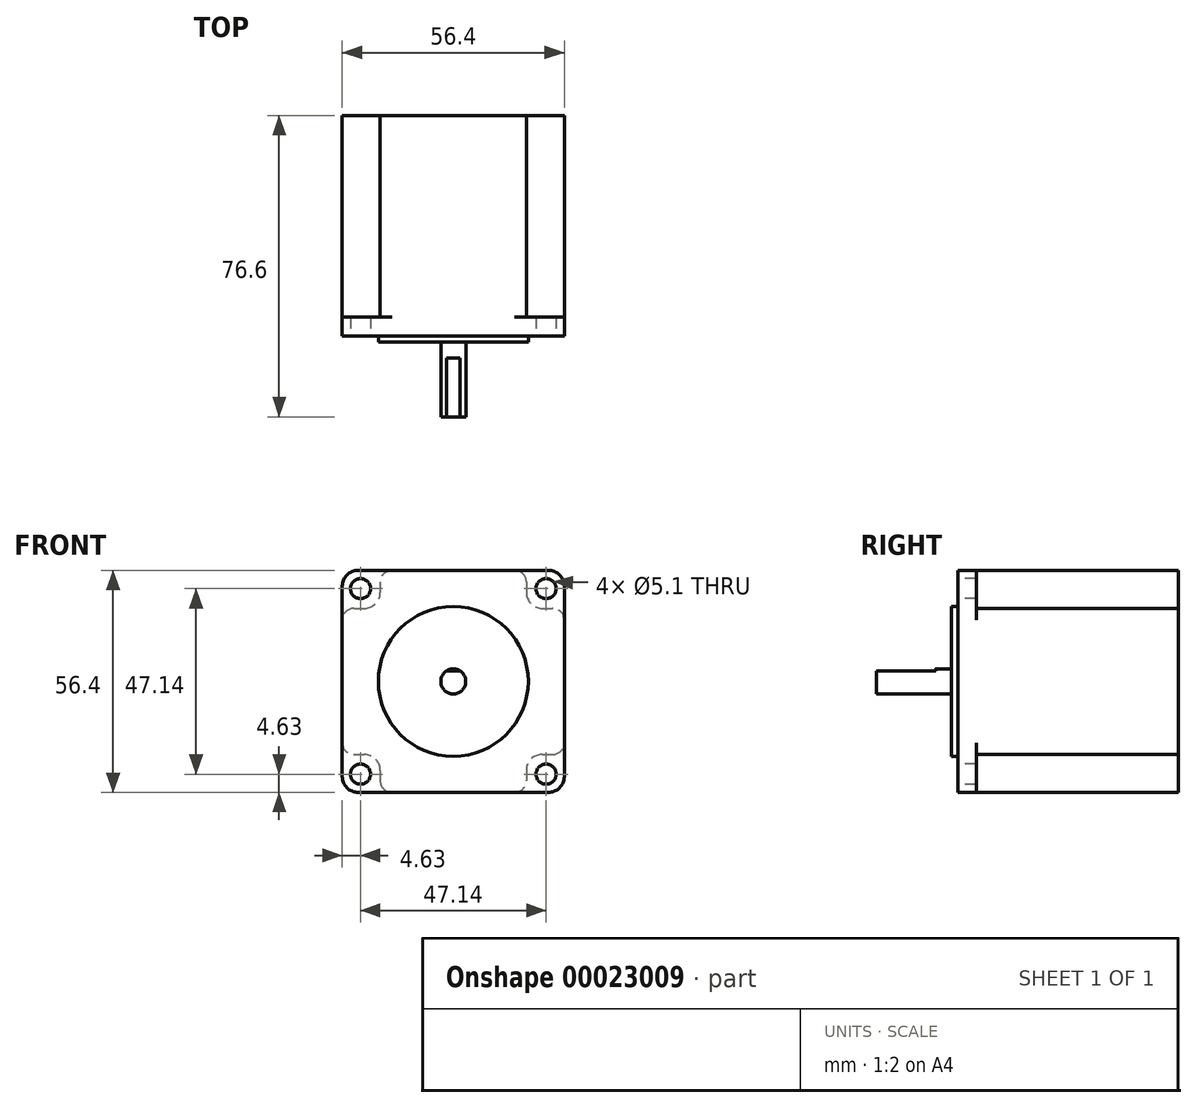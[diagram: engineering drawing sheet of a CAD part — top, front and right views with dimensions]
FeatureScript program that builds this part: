
annotation { "Feature Type Name" : "Feature", "Feature Type Description" : "" }
export const myFeature = defineFeature(function(context is Context, id is Id, definition is map)
    precondition{}
    {
        {
            var Q0;
            Q0=qCreatedBy(makeId("Front.planeOp"),FACE);
            var sketch = newSketch(context, id + "F0", { "sketchPlane" : qUnion([Q0])});
            skLineSegment(sketch, "E0.rect.bottom", {"start": v(-28.2, 28.2) * mm, "end": v(28.2, 28.2) * mm});
            skLineSegment(sketch, "E0.rect.top", {"start": v(-28.2, -28.2) * mm, "end": v(28.2, -28.2) * mm});
            skLineSegment(sketch, "E0.rect.left", {"start": v(-28.2, 28.2) * mm, "end": v(-28.2, -28.2) * mm});
            skLineSegment(sketch, "E0.rect.right", {"start": v(28.2, 28.2) * mm, "end": v(28.2, -28.2) * mm});
            skPoint(sketch, "E0.rect.middle", {"position": v(0, 0) * mm});
            skCircle(sketch, "E1", {"center": v(0, 0) * mm, "radius": 19.05 * mm});
            skCircle(sketch, "E2", {"center": v(0, 0) * mm, "radius": 3.17 * mm});
            skCircle(sketch, "E3", {"center": v(-23.57, 23.57) * mm, "radius": 2.55 * mm});
            skCircle(sketch, "E4", {"center": v(23.57, 23.57) * mm, "radius": 2.55 * mm});
            skCircle(sketch, "E5", {"center": v(23.57, -23.57) * mm, "radius": 2.55 * mm});
            skCircle(sketch, "E6", {"center": v(-23.57, -23.57) * mm, "radius": 2.55 * mm});
            skLineSegment(sketch, "E7.rect.bottom", {"start": v(-23.57, 23.57) * mm, "end": v(23.57, 23.57) * mm, "construction": true});
            skLineSegment(sketch, "E7.rect.top", {"start": v(-23.57, -23.57) * mm, "end": v(23.57, -23.57) * mm, "construction": true});
            skLineSegment(sketch, "E7.rect.left", {"start": v(-23.57, 23.57) * mm, "end": v(-23.57, -23.57) * mm, "construction": true});
            skLineSegment(sketch, "E7.rect.right", {"start": v(23.57, 23.57) * mm, "end": v(23.57, -23.57) * mm, "construction": true});
            skSolve(sketch);
        }
        {
            var Q0;
            Q0=makeQuery(id+"F0.imprint","IMPRINT",FACE,{"disambiguationData":[TD([[makeQuery(id+"F0.imprint","IMPRINT",EDGE,{"derivedFrom":sQuery(id+"F0.wireOp",EDGE,"E0.rect.bottom")}),-1.0]])]});
            var Q1;
            Q1=makeQuery(id+"F0.imprint","IMPRINT",FACE,{"disambiguationData":[TD([[makeQuery(id+"F0.imprint","IMPRINT",EDGE,{"derivedFrom":sQuery(id+"F0.wireOp",EDGE,"E1")}),1.0]])]});
            var Q2;
            Q2=makeQuery(id+"F0.imprint","IMPRINT",FACE,{"disambiguationData":[TD([[makeQuery(id+"F0.imprint","IMPRINT",EDGE,{"derivedFrom":sQuery(id+"F0.wireOp",EDGE,"E2")}),1.0]])]});
            extrude(context, id + "F1", {"entities" : qUnion([Q0, Q1, Q2]), "oppositeDirection" : true, "depth" : 4.8 * mm});
        }
        {
            var Q0;
            Q0=makeQuery(id+"F0.imprint","IMPRINT",FACE,{"disambiguationData":[TD([[makeQuery(id+"F0.imprint","IMPRINT",EDGE,{"derivedFrom":sQuery(id+"F0.wireOp",EDGE,"E1")}),1.0]])]});
            extrude(context, id + "F2", {"entities" : qUnion([Q0]), "operationType" : NewBodyOperationType.ADD, "depth" : 1.6 * mm});
        }
        {
            var Q0;
            Q0=makeQuery(id+"F0.imprint","IMPRINT",FACE,{"disambiguationData":[TD([[makeQuery(id+"F0.imprint","IMPRINT",EDGE,{"derivedFrom":sQuery(id+"F0.wireOp",EDGE,"E2")}),1.0]])]});
            extrude(context, id + "F3", {"entities" : qUnion([Q0]), "operationType" : NewBodyOperationType.ADD, "depth" : 20.6 * mm});
        }
        {
            var Q0;
            Q0=makeQuery(id+"F1.opExtrude","SWEPT_EDGE",EDGE,{"disambiguationData":[OSD([sQuery(id+"F0.wireOp",EDGE,"E0.rect.bottom"),sQuery(id+"F0.wireOp",EDGE,"E0.rect.left")])]});
            var Q1;
            Q1=makeQuery(id+"F1.opExtrude","SWEPT_EDGE",EDGE,{"disambiguationData":[OSD([sQuery(id+"F0.wireOp",EDGE,"E0.rect.bottom"),sQuery(id+"F0.wireOp",EDGE,"E0.rect.right")])]});
            var Q2;
            Q2=makeQuery(id+"F1.opExtrude","SWEPT_EDGE",EDGE,{"disambiguationData":[OSD([sQuery(id+"F0.wireOp",EDGE,"E0.rect.top"),sQuery(id+"F0.wireOp",EDGE,"E0.rect.right")])]});
            var Q3;
            Q3=makeQuery(id+"F1.opExtrude","SWEPT_EDGE",EDGE,{"disambiguationData":[OSD([sQuery(id+"F0.wireOp",EDGE,"E0.rect.top"),sQuery(id+"F0.wireOp",EDGE,"E0.rect.left")])]});
            fillet(context, id + "F4", {"entities" : qUnion([Q0, Q1, Q2, Q3]), "radius" : 4 * mm, "tangentPropagation" : true, "allowEdgeOverflow" : false});
        }
        {
            var Q0;
            Q0=makeQuery(id+"F1.opExtrude","SWEPT_FACE",FACE,{"disambiguationData":[OSD([sQuery(id+"F0.wireOp",EDGE,"E0.rect.left")])]});
            var sketch = newSketch(context, id + "F5", { "sketchPlane" : qUnion([Q0])});
            skLineSegment(sketch, "E8", {"start": v(1.6, 3.17) * mm, "end": v(20.6, 3.17) * mm});
            skLineSegment(sketch, "E9.0", {"start": v(20.6, 3.17) * mm, "end": v(20.6, -3.17) * mm});
            skLineSegment(sketch, "E10", {"start": v(5.6, 3.17) * mm, "end": v(5.6, 2.67) * mm});
            skLineSegment(sketch, "E11", {"start": v(5.6, 2.67) * mm, "end": v(20.6, 2.67) * mm});
            skSolve(sketch);
        }
        {
            var Q0;
            {var subQ1=sQuery(id+"F5.wireOp",EDGE,"E10");Q0=makeQuery(id+"F5.imprint","IMPRINT",FACE,{"disambiguationData":[TD([[makeQuery(id+"F5.imprint","IMPRINT",EDGE,{"derivedFrom":subQ1}),1.0]])]});}
            extrude(context, id + "F6", {"entities" : qUnion([Q0]), "operationType" : NewBodyOperationType.REMOVE, "endBound" : BoundingType.THROUGH_ALL, "oppositeDirection" : true, "depth" : 25 * mm});
        }
        {
            var Q0;
            Q0=qCreatedBy(makeId("Front.planeOp"),FACE);
            var sketch = newSketch(context, id + "F7", { "sketchPlane" : qUnion([Q0])});
            skPoint(sketch, "E12.rect.middle", {"position": v(0, 0.02) * mm});
            skPoint(sketch, "E13", {"position": v(0, 0) * mm});
            skLineSegment(sketch, "E14.rect.bottom", {"start": v(-18.57, 28.2) * mm, "end": v(18.57, 28.2) * mm});
            skLineSegment(sketch, "E14.rect.top", {"start": v(-18.57, -28.2) * mm, "end": v(18.57, -28.2) * mm});
            skLineSegment(sketch, "E14.rect.left", {"start": v(-18.57, 28.2) * mm, "end": v(-18.57, -28.2) * mm});
            skLineSegment(sketch, "E14.rect.right", {"start": v(18.57, 28.2) * mm, "end": v(18.57, -28.2) * mm});
            skLineSegment(sketch, "E15.rect.bottom", {"start": v(-28.2, 18.57) * mm, "end": v(28.2, 18.57) * mm});
            skLineSegment(sketch, "E15.rect.top", {"start": v(-28.2, -18.57) * mm, "end": v(28.2, -18.57) * mm});
            skLineSegment(sketch, "E15.rect.left", {"start": v(-28.2, 18.57) * mm, "end": v(-28.2, -18.57) * mm});
            skLineSegment(sketch, "E15.rect.right", {"start": v(28.2, 18.57) * mm, "end": v(28.2, -18.57) * mm});
            skSolve(sketch);
        }
        {
            var Q0;
            Q0=qSketchRegion(id+"F7",true);
            extrude(context, id + "F8", {"entities" : qUnion([Q0]), "operationType" : NewBodyOperationType.ADD, "oppositeDirection" : true, "depth" : 56 * mm});
        }
        {
            var Q0;
            Q0=makeQuery(id+"F8.opExtrude","SWEPT_EDGE",EDGE,{"disambiguationData":[OSD([sQuery(id+"F7.wireOp",EDGE,"E14.rect.right"),sQuery(id+"F7.wireOp",EDGE,"E15.rect.bottom")])]});
            var Q1;
            Q1=makeQuery(id+"F8.opExtrude","SWEPT_EDGE",EDGE,{"disambiguationData":[OSD([sQuery(id+"F7.wireOp",EDGE,"E14.rect.left"),sQuery(id+"F7.wireOp",EDGE,"E15.rect.bottom")])]});
            var Q2;
            Q2=makeQuery(id+"F8.opExtrude","SWEPT_EDGE",EDGE,{"disambiguationData":[OSD([sQuery(id+"F7.wireOp",EDGE,"E14.rect.left"),sQuery(id+"F7.wireOp",EDGE,"E15.rect.top")])]});
            var Q3;
            Q3=makeQuery(id+"F8.opExtrude","SWEPT_EDGE",EDGE,{"disambiguationData":[OSD([sQuery(id+"F7.wireOp",EDGE,"E14.rect.right"),sQuery(id+"F7.wireOp",EDGE,"E15.rect.top")])]});
            fillet(context, id + "F9", {"entities" : qUnion([Q0, Q1, Q2, Q3]), "radius" : 4 * mm, "tangentPropagation" : true, "allowEdgeOverflow" : false});
        }
        {
            var Q0;
            Q0=makeQuery(id+"F8.opExtrude","SWEPT_EDGE",EDGE,{"disambiguationData":[OSD([sQuery(id+"F7.wireOp",EDGE,"E14.rect.bottom"),sQuery(id+"F7.wireOp",EDGE,"E14.rect.right")])]});
            var Q1;
            Q1=makeQuery(id+"F8.opExtrude","SWEPT_EDGE",EDGE,{"disambiguationData":[OSD([sQuery(id+"F7.wireOp",EDGE,"E15.rect.bottom"),sQuery(id+"F7.wireOp",EDGE,"E15.rect.right")])]});
            var Q2;
            Q2=makeQuery(id+"F8.opExtrude","SWEPT_EDGE",EDGE,{"disambiguationData":[OSD([sQuery(id+"F7.wireOp",EDGE,"E15.rect.top"),sQuery(id+"F7.wireOp",EDGE,"E15.rect.right")])]});
            var Q3;
            Q3=makeQuery(id+"F8.opExtrude","SWEPT_EDGE",EDGE,{"disambiguationData":[OSD([sQuery(id+"F7.wireOp",EDGE,"E14.rect.top"),sQuery(id+"F7.wireOp",EDGE,"E14.rect.right")])]});
            var Q4;
            Q4=makeQuery(id+"F8.opExtrude","SWEPT_EDGE",EDGE,{"disambiguationData":[OSD([sQuery(id+"F7.wireOp",EDGE,"E14.rect.top"),sQuery(id+"F7.wireOp",EDGE,"E14.rect.left")])]});
            var Q5;
            Q5=makeQuery(id+"F8.opExtrude","SWEPT_EDGE",EDGE,{"disambiguationData":[OSD([sQuery(id+"F7.wireOp",EDGE,"E15.rect.top"),sQuery(id+"F7.wireOp",EDGE,"E15.rect.left")])]});
            var Q6;
            Q6=makeQuery(id+"F8.opExtrude","SWEPT_EDGE",EDGE,{"disambiguationData":[OSD([sQuery(id+"F7.wireOp",EDGE,"E15.rect.bottom"),sQuery(id+"F7.wireOp",EDGE,"E15.rect.left")])]});
            var Q7;
            Q7=makeQuery(id+"F8.opExtrude","SWEPT_EDGE",EDGE,{"disambiguationData":[OSD([sQuery(id+"F7.wireOp",EDGE,"E14.rect.bottom"),sQuery(id+"F7.wireOp",EDGE,"E14.rect.left")])]});
            fillet(context, id + "F10", {"entities" : qUnion([Q0, Q1, Q2, Q3, Q4, Q5, Q6, Q7]), "radius" : 3 * mm, "tangentPropagation" : true, "allowEdgeOverflow" : false});
        }
    });
